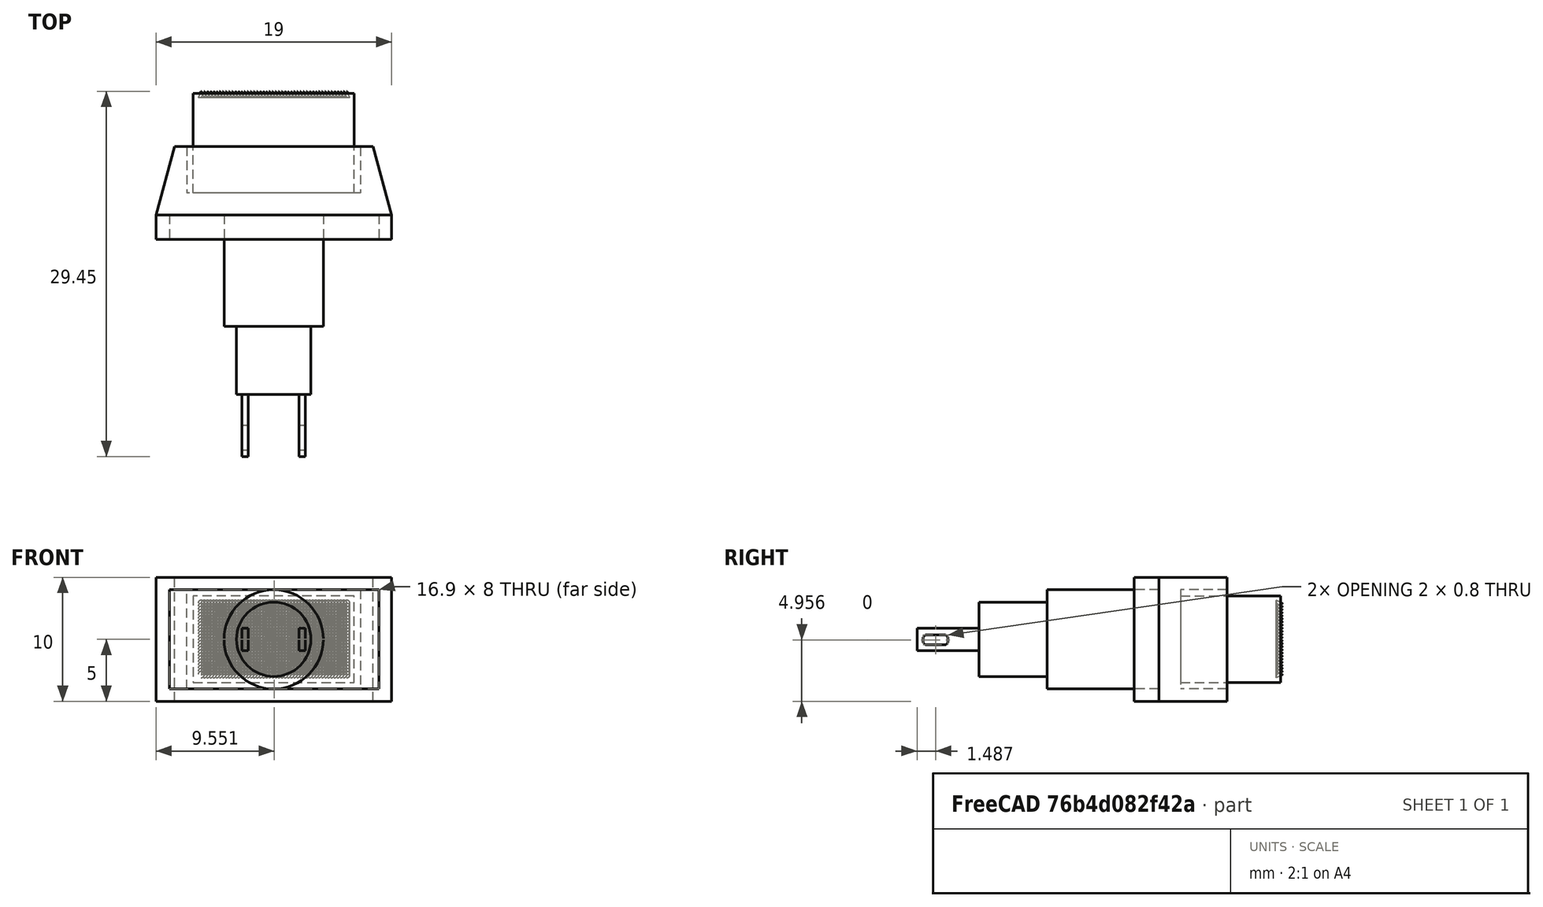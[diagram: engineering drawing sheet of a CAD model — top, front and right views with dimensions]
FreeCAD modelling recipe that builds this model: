
FCSTD DOCUMENT  (FreeCAD 0.18R16110 (Git))
Label: Miyama DS-462 3
License: All rights reserved
LicenseURL: http://en.wikipedia.org/wiki/All_rights_reserved
objects: Sketcher::SketchObject×11, Part::Extrusion×8, Part::Cut×3, Part::Cone×1, Part::FeaturePython×1, Part::Sweep×1
note: 25 computed .brp shape members not serialized (recipe doc carries the construction recipe); baked Part::Feature solids carry a one-line shape summary decoded from their .brp

FEATURE [Sketcher::SketchObject] Sketch
  sketch-geometry (12):
    g0: LineSegment [constr] StartX=-7 StartY=11.8 StartZ=0 EndX=7 EndY=11.8 EndZ=0
    g1: LineSegment [constr] StartX=-9.5 StartY=0 StartZ=0 EndX=9.5 EndY=0 EndZ=0
    g2: LineSegment [constr] StartX=-7 StartY=11.8 StartZ=0 EndX=-7 EndY=7.5 EndZ=0
    g3: LineSegment [constr] StartX=7 StartY=7.5 StartZ=0 EndX=7 EndY=11.8 EndZ=0
    g4: LineSegment [constr] StartX=9.5 StartY=0 StartZ=0 EndX=9.5 EndY=2 EndZ=0
    g5: LineSegment [constr] StartX=9.5 StartY=2 StartZ=0 EndX=7 EndY=7.5 EndZ=0
    g6: LineSegment [constr] StartX=-9.5 StartY=0 StartZ=0 EndX=-9.5 EndY=2 EndZ=0
    g7: LineSegment [constr] StartX=-9.5 StartY=2 StartZ=0 EndX=-7 EndY=7.5 EndZ=0
    g8: LineSegment StartX=-9.5 StartY=2 StartZ=0 EndX=-9.5 EndY=0 EndZ=0
    g9: LineSegment StartX=-9.5 StartY=0 StartZ=0 EndX=9.5 EndY=0 EndZ=0
    g10: LineSegment StartX=9.5 StartY=0 StartZ=0 EndX=9.5 EndY=2 EndZ=0
    g11: LineSegment StartX=9.5 StartY=2 StartZ=0 EndX=-9.5 EndY=2 EndZ=0
  constraints (31):
    c: DistanceX(g0,g0) = 14
    c: DistanceX(g1,g1) = 19
    c: Symmetric(g0,g0,g-2)
    c: Coincident(g2,g0)
    c: Vertical(g2)
    c: Coincident(g3,g0)
    c: Vertical(g3)
    c: DistanceY(g3,g3) = 4.3
    c: Coincident(g4,g1)
    c: Coincident(g5,g4)
    c: Coincident(g7,g6)
    c: Coincident(g7,g2)
    c: Vertical(g6)
    c: Vertical(g4)
    c: DistanceY(g1,g5) = 7.5
    c: Equal(g4,g6)
    c: Coincident(g6,g1)
    c: DistanceY(g4,g4) = 2
    c: PointOnObject(g-1,g1)
    c: Horizontal(g1)
    c: Equal(g7,g5)
    c: Coincident(g3,g5)
    c: Equal(g3,g2)
    c: Coincident(g6,g8)
    c: Coincident(g8,g1)
    c: Coincident(g8,g9)
    c: Coincident(g9,g1)
    c: Coincident(g9,g10)
    c: Coincident(g10,g4)
    c: Coincident(g10,g11)
    c: Coincident(g11,g8)
FEATURE [Sketcher::SketchObject] Sketch001
  sketch-geometry (12):
    g0: LineSegment [constr] StartX=-8 StartY=11.8 StartZ=0 EndX=8 EndY=11.8 EndZ=0
    g1: LineSegment [constr] StartX=-9.5 StartY=0 StartZ=0 EndX=9.5 EndY=0 EndZ=0
    g2: LineSegment [constr] StartX=-8 StartY=11.8 StartZ=0 EndX=-8 EndY=7.5 EndZ=0
    g3: LineSegment [constr] StartX=8 StartY=7.5 StartZ=0 EndX=8 EndY=11.8 EndZ=0
    g4: LineSegment [constr] StartX=9.5 StartY=0 StartZ=0 EndX=9.5 EndY=2 EndZ=0
    g5: LineSegment [constr] StartX=9.5 StartY=2 StartZ=0 EndX=8 EndY=7.5 EndZ=0
    g6: LineSegment [constr] StartX=-9.5 StartY=0 StartZ=0 EndX=-9.5 EndY=2 EndZ=0
    g7: LineSegment [constr] StartX=-9.5 StartY=2 StartZ=0 EndX=-8 EndY=7.5 EndZ=0
    g8: LineSegment StartX=-9.5 StartY=2 StartZ=0 EndX=-8 EndY=7.5 EndZ=0
    g9: LineSegment StartX=-8 StartY=7.5 StartZ=0 EndX=8 EndY=7.5 EndZ=0
    g10: LineSegment StartX=8 StartY=7.5 StartZ=0 EndX=9.5 EndY=2 EndZ=0
    g11: LineSegment StartX=9.5 StartY=2 StartZ=0 EndX=-9.5 EndY=2 EndZ=0
  constraints (31):
    c: DistanceX(g0,g0) = 16
    c: DistanceX(g1,g1) = 19
    c: Symmetric(g0,g0,g-2)
    c: Coincident(g2,g0)
    c: Vertical(g2)
    c: Coincident(g3,g0)
    c: Vertical(g3)
    c: DistanceY(g3,g3) = 4.3
    c: Coincident(g4,g1)
    c: Coincident(g5,g4)
    c: Coincident(g7,g6)
    c: Coincident(g7,g2)
    c: Vertical(g6)
    c: Vertical(g4)
    c: DistanceY(g1,g5) = 7.5
    c: Equal(g4,g6)
    c: Coincident(g6,g1)
    c: DistanceY(g4,g4) = 2
    c: PointOnObject(g-1,g1)
    c: Horizontal(g1)
    c: Equal(g7,g5)
    c: Coincident(g3,g5)
    c: Equal(g3,g2)
    c: Coincident(g6,g8)
    c: Coincident(g8,g2)
    c: Coincident(g8,g9)
    c: Coincident(g9,g10)
    c: Coincident(g10,g4)
    c: Coincident(g10,g11)
    c: Coincident(g11,g8)
    c: Coincident(g9,g3)
FEATURE [Sketcher::SketchObject] Sketch002
  sketch-geometry (12):
    g0: LineSegment [constr] StartX=-7 StartY=11.8 StartZ=0 EndX=7 EndY=11.8 EndZ=0
    g1: LineSegment [constr] StartX=-9.5 StartY=0 StartZ=0 EndX=9.5 EndY=0 EndZ=0
    g2: LineSegment [constr] StartX=-7 StartY=11.8 StartZ=0 EndX=-7 EndY=7.5 EndZ=0
    g3: LineSegment [constr] StartX=7 StartY=7.5 StartZ=0 EndX=7 EndY=11.8 EndZ=0
    g4: LineSegment [constr] StartX=9.5 StartY=0 StartZ=0 EndX=9.5 EndY=2 EndZ=0
    g5: LineSegment [constr] StartX=9.5 StartY=2 StartZ=0 EndX=7 EndY=7.5 EndZ=0
    g6: LineSegment [constr] StartX=-9.5 StartY=0 StartZ=0 EndX=-9.5 EndY=2 EndZ=0
    g7: LineSegment [constr] StartX=-9.5 StartY=2 StartZ=0 EndX=-7 EndY=7.5 EndZ=0
    g8: LineSegment StartX=-7 StartY=11.8 StartZ=0 EndX=-7 EndY=7.5 EndZ=0
    g9: LineSegment StartX=-7 StartY=7.5 StartZ=0 EndX=7 EndY=7.5 EndZ=0
    g10: LineSegment StartX=7 StartY=7.5 StartZ=0 EndX=7 EndY=11.8 EndZ=0
    g11: LineSegment StartX=7 StartY=11.8 StartZ=0 EndX=-7 EndY=11.8 EndZ=0
  constraints (31):
    c: DistanceX(g0,g0) = 14
    c: DistanceX(g1,g1) = 19
    c: Symmetric(g0,g0,g-2)
    c: Coincident(g2,g0)
    c: Vertical(g2)
    c: Coincident(g3,g0)
    c: Vertical(g3)
    c: DistanceY(g3,g3) = 4.3
    c: Coincident(g4,g1)
    c: Coincident(g5,g4)
    c: Coincident(g7,g6)
    c: Coincident(g7,g2)
    c: Vertical(g6)
    c: Vertical(g4)
    c: DistanceY(g1,g5) = 7.5
    c: Equal(g4,g6)
    c: Coincident(g6,g1)
    c: DistanceY(g4,g4) = 2
    c: PointOnObject(g-1,g1)
    c: Horizontal(g1)
    c: Equal(g7,g5)
    c: Coincident(g3,g5)
    c: Equal(g3,g2)
    c: Coincident(g0,g8)
    c: Coincident(g8,g2)
    c: Coincident(g8,g9)
    c: Coincident(g9,g3)
    c: Coincident(g9,g10)
    c: Coincident(g10,g0)
    c: Coincident(g10,g11)
    c: Coincident(g11,g8)
FEATURE [Part::Extrusion] Extrude
  Base = -> Sketch
  Dir = (0,0,1)
  DirMode = 2
  FaceMakerClass = Part::FaceMakerBullseye
  LengthFwd = 10
  LengthRev = 0
  Solid = true
  Symmetric = false
FEATURE [Part::Extrusion] Extrude001
  Base = -> Sketch001
  Dir = (0,0,1)
  DirMode = 2
  FaceMakerClass = Part::FaceMakerBullseye
  LengthFwd = 10
  LengthRev = 0
  Solid = true
  Symmetric = false
FEATURE [Sketcher::SketchObject] Sketch003
  MapMode = 5
  Placement = pos=(0,7.5,0) rot=(0,0.707107,0.707107;3.14159rad)
  Support = -> [Extrude001]
  sketch-geometry (4):
    g0: LineSegment StartX=-7 StartY=9 StartZ=0 EndX=-7 EndY=1 EndZ=0
    g1: LineSegment StartX=-7 StartY=1 StartZ=0 EndX=7 EndY=1 EndZ=0
    g2: LineSegment StartX=7 StartY=1 StartZ=0 EndX=7 EndY=9 EndZ=0
    g3: LineSegment StartX=7 StartY=9 StartZ=0 EndX=-7 EndY=9 EndZ=0
  constraints (8):
    c: Vertical(g0)
    c: Coincident(g0,g1)
    c: Horizontal(g1)
    c: Coincident(g1,g2)
    c: Vertical(g2)
    c: Coincident(g2,g3)
    c: Coincident(g3,g0)
    c: Horizontal(g3)
FEATURE [Part::Extrusion] Extrude002
  Base = -> Sketch003
  Dir = (0,1,-2e-16)
  DirMode = 2
  FaceMakerClass = Part::FaceMakerBullseye
  LengthFwd = -7.5
  LengthRev = 0
  Solid = true
  Symmetric = true
FEATURE [Part::Cut] Cut
  Base = -> Extrude001
  Tool = -> Extrude002
FEATURE [Sketcher::SketchObject] Sketch004
  MapMode = 5
  Placement = pos=(0,3.75,-8e-16) rot=(0,0.707107,0.707107;3.14159rad)
  Support = -> [Cut]
  sketch-geometry (4):
    g0: LineSegment StartX=-6.5 StartY=8.5 StartZ=0 EndX=6.5 EndY=8.5 EndZ=0
    g1: LineSegment StartX=6.5 StartY=8.5 StartZ=0 EndX=6.5 EndY=1.5 EndZ=0
    g2: LineSegment StartX=6.5 StartY=1.5 StartZ=0 EndX=-6.5 EndY=1.5 EndZ=0
    g3: LineSegment StartX=-6.5 StartY=1.5 StartZ=0 EndX=-6.5 EndY=8.5 EndZ=0
  constraints (8):
    c: Coincident(g0,g1)
    c: Coincident(g1,g2)
    c: Coincident(g2,g3)
    c: Coincident(g3,g0)
    c: Horizontal(g0)
    c: Horizontal(g2)
    c: Vertical(g1)
    c: Vertical(g3)
FEATURE [Part::Extrusion] Extrude003
  Base = -> Sketch004
  Dir = (0,1,-2e-16)
  DirMode = 2
  FaceMakerClass = Part::FaceMakerBullseye
  LengthFwd = 8.05
  LengthRev = 0
  Solid = true
  Symmetric = false
FEATURE [Part::Cone] Cone
  Angle = 360
  AttacherType = Attacher::AttachEngine3D
  Height = 0.5
  Placement = pos=(-5.85,11.45,7.9) rot=(-1,0,0;1.5708rad)
  Radius1 = 0.25
  Radius2 = 0.01
FEATURE [Part::FeaturePython] Array  # Draft array (typed FeaturePython)
  Angle = 360
  ArrayType = 0
  Axis = (0,0,1)
  Base = -> Cone
  Center = (0,0,0)
  Fuse = false
  IntervalAxis = (0,0,0)
  IntervalX = (0.25,0,0)
  IntervalY = (0,1,0)
  IntervalZ = (0,0,-0.25)
  NumberPolar = 1
  NumberX = 48
  NumberY = 1
  NumberZ = 24
FEATURE [Sketcher::SketchObject] Sketch005
  MapMode = 5
  Placement = pos=(0,0,0) rot=(1,0,0;1.5708rad)
  Support = -> [Extrude]
  sketch-geometry (4):
    g0: LineSegment StartX=-8.39842 StartY=9 StartZ=0 EndX=8.5 EndY=9 EndZ=0
    g1: LineSegment StartX=8.5 StartY=9 StartZ=0 EndX=8.5 EndY=1 EndZ=0
    g2: LineSegment StartX=8.5 StartY=1 StartZ=0 EndX=-8.39842 EndY=1 EndZ=0
    g3: LineSegment StartX=-8.39842 StartY=1 StartZ=0 EndX=-8.39842 EndY=9 EndZ=0
  constraints (8):
    c: Coincident(g0,g1)
    c: Coincident(g1,g2)
    c: Coincident(g2,g3)
    c: Coincident(g3,g0)
    c: Horizontal(g0)
    c: Horizontal(g2)
    c: Vertical(g1)
    c: Vertical(g3)
FEATURE [Part::Extrusion] Extrude004
  Base = -> Sketch005
  Dir = (0,-1,2e-16)
  DirMode = 2
  FaceMakerClass = Part::FaceMakerBullseye
  LengthFwd = 5
  LengthRev = 0
  Solid = true
  Symmetric = true
FEATURE [Part::Cut] Cut001
  Base = -> Extrude
  Tool = -> Extrude004
FEATURE [Sketcher::SketchObject] Sketch006
  MapMode = 5
  Placement = pos=(0,2,0) rot=(1,0,0;1.5708rad)
  Support = -> [Cut]
  sketch-geometry (1):
    g0: Circle CenterX=0 CenterY=5 CenterZ=0 NormalX=0 NormalY=0 NormalZ=1 AngleXU=0 Radius=4
  constraints (2):
    c: PointOnObject(g0,g-2)
    c: Radius(g0) = 4
FEATURE [Sketcher::SketchObject] Sketch007
  ExternalGeometry = -> [Cut]
  sketch-geometry (1):
    g0: LineSegment StartX=0 StartY=2 StartZ=0 EndX=0 EndY=-7 EndZ=0
  constraints (1):
    c: DistanceY(g0,g0) = 9
FEATURE [Part::Sweep] Sweep
  Frenet = false
  Sections = -> [Sketch006]
  Solid = true
  Spine = -> Sketch007
  Transition = 1
FEATURE [Sketcher::SketchObject] Sketch008
  MapMode = 5
  Placement = pos=(0,-7,0) rot=(1,0,0;1.5708rad)
  Support = -> [Sweep]
  sketch-geometry (1):
    g0: Circle CenterX=0 CenterY=5 CenterZ=0 NormalX=0 NormalY=0 NormalZ=1 AngleXU=0 Radius=3
  constraints (1):
    c: PointOnObject(g0,g-2)
FEATURE [Part::Extrusion] Extrude005
  Base = -> Sketch008
  Dir = (0,-1,2e-16)
  DirMode = 2
  FaceMakerClass = Part::FaceMakerBullseye
  LengthFwd = 5.5
  LengthRev = 0
  Solid = true
  Symmetric = false
FEATURE [Sketcher::SketchObject] Sketch009
  MapMode = 5
  Placement = pos=(-1.2e-15,-12.5,2.1e-15) rot=(1,0,0;1.5708rad)
  Support = -> [Extrude005]
  sketch-geometry (10):
    g0: LineSegment StartX=-2.55 StartY=5.89295 StartZ=0 EndX=-2.05 EndY=5.89295 EndZ=0
    g1: LineSegment StartX=-2.05 StartY=5.89295 StartZ=0 EndX=-2.05 EndY=4.09295 EndZ=0
    g2: LineSegment StartX=-2.05 StartY=4.09295 StartZ=0 EndX=-2.55 EndY=4.09295 EndZ=0
    g3: LineSegment StartX=-2.55 StartY=4.09295 StartZ=0 EndX=-2.55 EndY=5.89295 EndZ=0
    g4: LineSegment [constr] StartX=0 StartY=10 StartZ=0 EndX=0 EndY=0 EndZ=0
    g5: LineSegment [constr] StartX=-9.45869 StartY=4.99295 StartZ=0 EndX=9.50951 EndY=4.99295 EndZ=0
    g6: LineSegment StartX=2.55 StartY=5.89295 StartZ=0 EndX=2.55 EndY=4.09295 EndZ=0
    g7: LineSegment StartX=2.05 StartY=5.89295 StartZ=0 EndX=2.55 EndY=5.89295 EndZ=0
    g8: LineSegment StartX=2.05 StartY=4.09295 StartZ=0 EndX=2.05 EndY=5.89295 EndZ=0
    g9: LineSegment StartX=2.55 StartY=4.09295 StartZ=0 EndX=2.05 EndY=4.09295 EndZ=0
  constraints (27):
    c: Coincident(g0,g1)
    c: Coincident(g1,g2)
    c: Coincident(g2,g3)
    c: Coincident(g3,g0)
    c: Horizontal(g0)
    c: Horizontal(g2)
    c: Vertical(g1)
    c: Vertical(g3)
    c: DistanceX(g0,g0) = 0.5
    c: DistanceY(g1,g1) = 1.8
    c: PointOnObject(g4,g-2)
    c: Coincident(g4,g-1)
    c: Horizontal(g5)
    c: DistanceY(g5,g0) = 0.9
    c: DistanceX(g1,g-1) = 2.05
    c: Coincident(g7,g6)
    c: Coincident(g6,g9)
    c: Coincident(g9,g8)
    c: Coincident(g8,g7)
    c: Horizontal(g7)
    c: Horizontal(g9)
    c: Vertical(g6)
    c: Vertical(g8)
    c: DistanceX(g7,g7) = 0.5
    c: DistanceY(g6,g6) = 1.8
    c: DistanceX(g-1,g8) = 2.05
    c: DistanceY(g5,g7) = 0.9
FEATURE [Part::Extrusion] Extrude006
  Base = -> Sketch009
  Dir = (-1e-16,-1,2e-16)
  DirMode = 2
  FaceMakerClass = Part::FaceMakerBullseye
  LengthFwd = 5
  LengthRev = 0
  Solid = true
  Symmetric = false
FEATURE [Sketcher::SketchObject] Sketch010
  MapMode = 5
  Placement = pos=(2.55,-3e-16,0) rot=(0.57735,0.57735,0.57735;2.0944rad)
  Support = -> [Extrude006]
  sketch-geometry (9):
    g0: LineSegment StartX=-16.7272 StartY=5.35582 StartZ=0 EndX=-15.2992 EndY=5.35582 EndZ=0
    g1: LineSegment StartX=-15.0132 StartY=5.06984 StartZ=0 EndX=-15.0132 EndY=4.8418 EndZ=0
    g2: LineSegment StartX=-15.2992 StartY=4.55582 StartZ=0 EndX=-16.7272 EndY=4.55582 EndZ=0
    g3: LineSegment StartX=-17.0132 StartY=4.8418 StartZ=0 EndX=-17.0132 EndY=5.06984 EndZ=0
    g4: LineSegment [constr] StartX=-17.5132 StartY=4 StartZ=0 EndX=-17.5132 EndY=5 EndZ=0
    g5: ArcOfCircle CenterX=-15.2992 CenterY=5.06984 CenterZ=0 NormalX=0 NormalY=0 NormalZ=1 AngleXU=0 Radius=0.285978 StartAngle=1.3e-15 EndAngle=1.5708
    g6: ArcOfCircle CenterX=-16.7272 CenterY=5.06984 CenterZ=0 NormalX=0 NormalY=0 NormalZ=1 AngleXU=0 Radius=0.285978 StartAngle=1.5708 EndAngle=3.14159
    g7: ArcOfCircle CenterX=-15.2992 CenterY=4.8418 CenterZ=0 NormalX=0 NormalY=0 NormalZ=1 AngleXU=0 Radius=0.285978 StartAngle=4.71239 EndAngle=6.28319
    g8: ArcOfCircle CenterX=-16.7272 CenterY=4.8418 CenterZ=0 NormalX=0 NormalY=0 NormalZ=1 AngleXU=0 Radius=0.285978 StartAngle=3.14159 EndAngle=4.71239
  constraints (21):
    c: Horizontal(g0)
    c: Horizontal(g2)
    c: Vertical(g1)
    c: Vertical(g3)
    c: Vertical(g4)
    c: DistanceX(g4) = -17.5132
    c: DistanceY(g4) = 5
    c: Tangent(g1,g5) = 1.5708
    c: Tangent(g0,g5) = 1.5708
    c: Tangent(g0,g6) = 1.5708
    c: Tangent(g3,g6) = 1.5708
    c: Tangent(g1,g7) = 1.5708
    c: Tangent(g2,g7) = 1.5708
    c: Tangent(g2,g8) = 1.5708
    c: Tangent(g3,g8) = 1.5708
    c: DistanceX(g6,g8) = 0
    c: DistanceX(g5,g7) = 0
    c: DistanceX(g4,g3) = 0.5
    c: Equal(g6,g5)
    c: DistanceY(g2,g0) = 0.8
    c: DistanceX(g3,g1) = 2
FEATURE [Part::Extrusion] Extrude007
  Base = -> Sketch010
  Dir = (1,0,0)
  DirMode = 2
  FaceMakerClass = Part::FaceMakerBullseye
  LengthFwd = 20
  LengthRev = 0
  Reversed = true
  Solid = true
  Symmetric = true
FEATURE [Part::Cut] Cut002
  Base = -> Extrude006
  Tool = -> Extrude007
